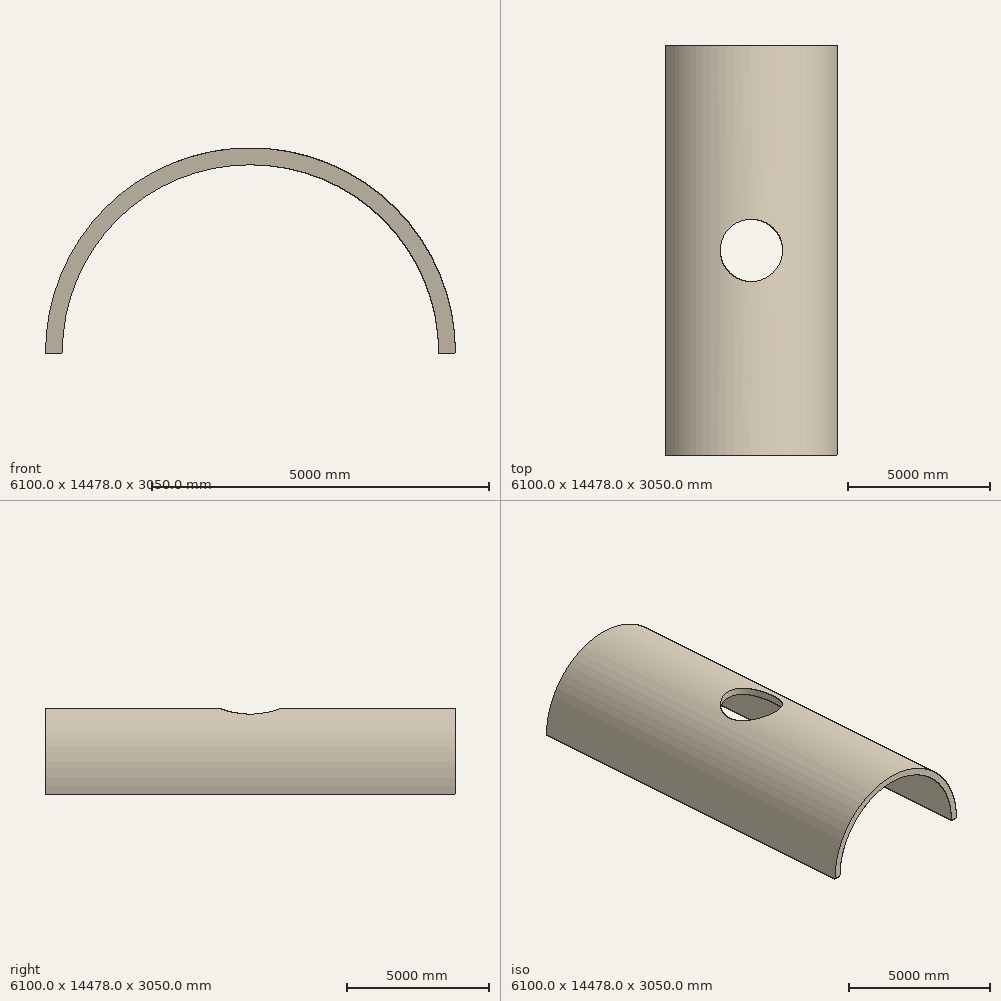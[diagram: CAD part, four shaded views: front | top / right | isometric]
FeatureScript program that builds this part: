
annotation { "Feature Type Name" : "Feature", "Feature Type Description" : "" }
export const myFeature = defineFeature(function(context is Context, id is Id, definition is map)
    precondition{}
    {
        {
            var Q0;
            Q0=qCreatedBy(makeId("Front.planeOp"),FACE);
            var sketch = newSketch(context, id + "F0", { "sketchPlane" : qUnion([Q0])});
            skCircle(sketch, "E0", {"center": v(0, 0) * mm, "radius": 3050 * mm});
            skCircle(sketch, "E1", {"center": v(0, 0) * mm, "radius": 2800 * mm});
            skSolve(sketch);
        }
        {
            var Q0;
            Q0=makeQuery(id+"F0.imprint","IMPRINT",FACE,{"disambiguationData":[TD([[makeQuery(id+"F0.imprint","IMPRINT",EDGE,{"derivedFrom":sQuery(id+"F0.wireOp",EDGE,"E0")}),1.0]])]});
            extrude(context, id + "F1", {"entities" : qUnion([Q0]), "depth" : 14478 * mm});
        }
        {
            var Q0;
            Q0=makeQuery(id+"F1.opExtrude","CAP_FACE",FACE,{"disambiguationData":[OSD([sQuery(id+"F0.wireOp",EDGE,"E0"),sQuery(id+"F0.wireOp",EDGE,"E1")])],"isStart":false});
            cPlane(context, id + "F2", {"entities" : qUnion([Q0]), "cplaneType" : CPlaneType.OFFSET, "offset" : 0 * mm, "width" : 150 * mm, "height" : 150 * mm});
        }
        {
            var Q0;
            Q0=qCreatedBy(id+"F2.planeOp",FACE);
            var sketch = newSketch(context, id + "F3", { "sketchPlane" : qUnion([Q0])});
            skLineSegment(sketch, "E2.bottom", {"start": v(-3484.89, 0) * mm, "end": v(3396.42, 0) * mm});
            skLineSegment(sketch, "E2.top", {"start": v(-3484.89, -3431.65) * mm, "end": v(3396.42, -3431.65) * mm});
            skLineSegment(sketch, "E2.left", {"start": v(-3484.89, 0) * mm, "end": v(-3484.89, -3431.65) * mm});
            skLineSegment(sketch, "E2.right", {"start": v(3396.42, 0) * mm, "end": v(3396.42, -3431.65) * mm});
            skSolve(sketch);
        }
        {
            var Q0;
            Q0=makeQuery(id+"F3.imprint","IMPRINT",FACE,{"disambiguationData":[TD([[makeQuery(id+"F3.imprint","IMPRINT",EDGE,{"derivedFrom":sQuery(id+"F3.wireOp",EDGE,"E2.bottom")}),-1.0]])]});
            extrude(context, id + "F4", {"entities" : qUnion([Q0]), "operationType" : NewBodyOperationType.REMOVE, "oppositeDirection" : true, "depth" : 15000 * mm});
        }
        {
            var Q0;
            Q0=qCreatedBy(makeId("Top.planeOp"),FACE);
            var sketch = newSketch(context, id + "F5", { "sketchPlane" : qUnion([Q0])});
            skCircle(sketch, "E3", {"center": v(0, -7239) * mm, "radius": 1100 * mm});
            skSolve(sketch);
        }
        {
            var Q0;
            Q0 = qSketchRegion(id + "F5", true);
            extrude(context, id + "F6", {"entities" : qUnion([Q0]), "operationType" : NewBodyOperationType.REMOVE, "depth" : 10000 * mm});
        }
    });
